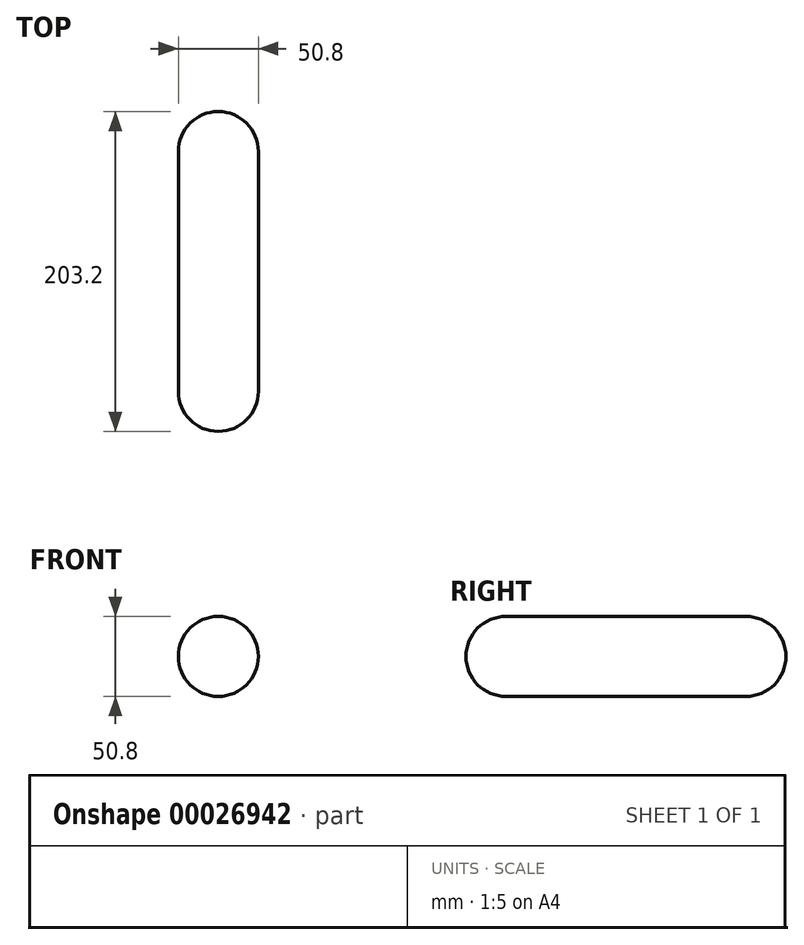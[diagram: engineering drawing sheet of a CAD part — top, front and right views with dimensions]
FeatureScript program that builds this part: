
annotation { "Feature Type Name" : "Feature", "Feature Type Description" : "" }
export const myFeature = defineFeature(function(context is Context, id is Id, definition is map)
    precondition{}
    {
        {
            var Q0;
            Q0=qCreatedBy(makeId("Front.planeOp"),FACE);
            var sketch = newSketch(context, id + "F0", { "sketchPlane" : qUnion([Q0])});
            skCircle(sketch, "E0", {"center": v(-13.09, 11.62) * mm, "radius": 25.4 * mm});
            skLineSegment(sketch, "E1", {"start": v(-13.09, -13.78) * mm, "end": v(-13.09, 37.02) * mm});
            skSolve(sketch);
        }
        {
            var Q0;
            {var subQ0=sQuery(id+"F0.wireOp",EDGE,"E1");Q0=makeQuery(id+"F0.imprint","IMPRINT",FACE,{"disambiguationData":[TD([[makeQuery(id+"F0.imprint","IMPRINT",EDGE,{"derivedFrom":subQ0}),-1.0]])]});}
            var Q1;
            Q1=sQuery(id+"F0.wireOp",EDGE,"E1");
            revolve(context, id + "F1", {"entities" : qUnion([Q0]), "axis" : qUnion([Q1]), "revolveType" : RevolveType.ONE_DIRECTION, "angle" : 180 * degree});
        }
        {
            var Q0;
            Q0=makeQuery(id+"F1.opRevolve","CAP_FACE",FACE,{"disambiguationData":[OSD([sQuery(id+"F0.wireOp",EDGE,"E0"),sQuery(id+"F0.wireOp",EDGE,"E1")])],"isStart":true});
            extrude(context, id + "F2", {"entities" : qUnion([Q0]), "operationType" : NewBodyOperationType.ADD, "depth" : 76.2 * mm});
        }
        {
            var Q0;
            Q0=makeQuery(id+"F1.opRevolve","SWEPT_BODY",BODY,{"disambiguationData":[OSD([sQuery(id+"F0.wireOp",EDGE,"E0"),sQuery(id+"F0.wireOp",EDGE,"E1")])]});
            var Q1;
            Q1=makeQuery(id+"F2.opExtrude","CAP_FACE",FACE,{"disambiguationData":[OSD([sQuery(id+"F0.wireOp",EDGE,"E0"),sQuery(id+"F0.wireOp",EDGE,"E1")])],"isStart":false});
            mirror(context, id + "F3", {"operationType" : NewBodyOperationType.ADD, "entities" : qUnion([Q0]), "mirrorPlane" : qUnion([Q1])});
        }
    });
